# Revit family: Drinking_Fountain-Haws_Corporation-Bottle_Filler_1900 new
name_source: partatom
category: Plumbing Fixtures
revit_build: Autodesk Revit Architecture 2015 (Build: 20160512_1515(x64)
units: mm (PartAtom-declared; Revit-internal decimal feet)

## types (3) — shared parameters
Apparent Load = 0 VA
Assembly Code = D2010800
Cost Note = For Cost information please visit the Resource tab in the Product Page URL
Default Elevation = 2' - 6"
Depth = 0' - 4"
Description = Bottle Filler
Flow = 0 GPM
Frequency = 60 Hz
Height = 1' - 4 1/4"
Installation Instructions = https://www.hawsco.com
Manufacturer = Haws Corporation
Model = 1900
Number of Poles = 1
Panel Finish = Plastic-Haws-Grey
Phase = 1
Power Factor = 1
Product Documentation Link = https://www.hawsco.com
Product Page URL = https://www.hawsco.com
Sanitary Radius = 0' - 1 1/4"
Series = 1900
Supply Radius = 0' - 0 1/8"
Type Comments = Surface Mounted
URL = http://www.hawsco.com
Version = 2014-v2.0a
Voltage = 0 V
Width = 0' - 8 5/16"
zero-valued in all types: CWFU, Cost, HWFU, WFU

## per-type parameters (varying)
| type | Drain Basin | Reverse Drain Basin |
| Bottler Filler w/ Drain Basin | Yes | No |
| Bottle Filler | No | No |
| Bottle Filler w/ Reverse Drain Basin | No | Yes |

## geometry (parser evidence)
native form markers: Blend x8, Sweep x3
no freeform markers — native parametric forms only
